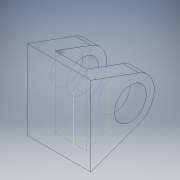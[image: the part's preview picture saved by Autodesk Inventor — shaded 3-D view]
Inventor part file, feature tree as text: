
AUTODESK INVENTOR PART (.ipt)
format: ipt  version: 2018 (Build 220112000, 112)  size: 124,928 bytes
history: native  units: mm
features: extrude x2, sketch x2, plane x1
ambient origin geometry x8: Origin, YZ Plane, XZ Plane, XY Plane, X Axis, Y Axis, Z Axis, Center Point
bodies: Solid1 (feature_tree)
feature tree (5):
  extrude  "Extrusion1"  Depth=50.0mm
  plane  "Work Plane1"
  extrude  "Extrusion2"  Depth=60.0mm
  sketch  "Sketch1"  dims[d0=100.0mm d1=50.0mm]
  sketch  "Sketch2"  dims[d2=40.0mm d3=60.0mm d5=12.217305mm d6=12.217305mm d7=80.0mm d8=0.0mm d9=-20.0mm d10=40.0mm d11=0.0mm]
